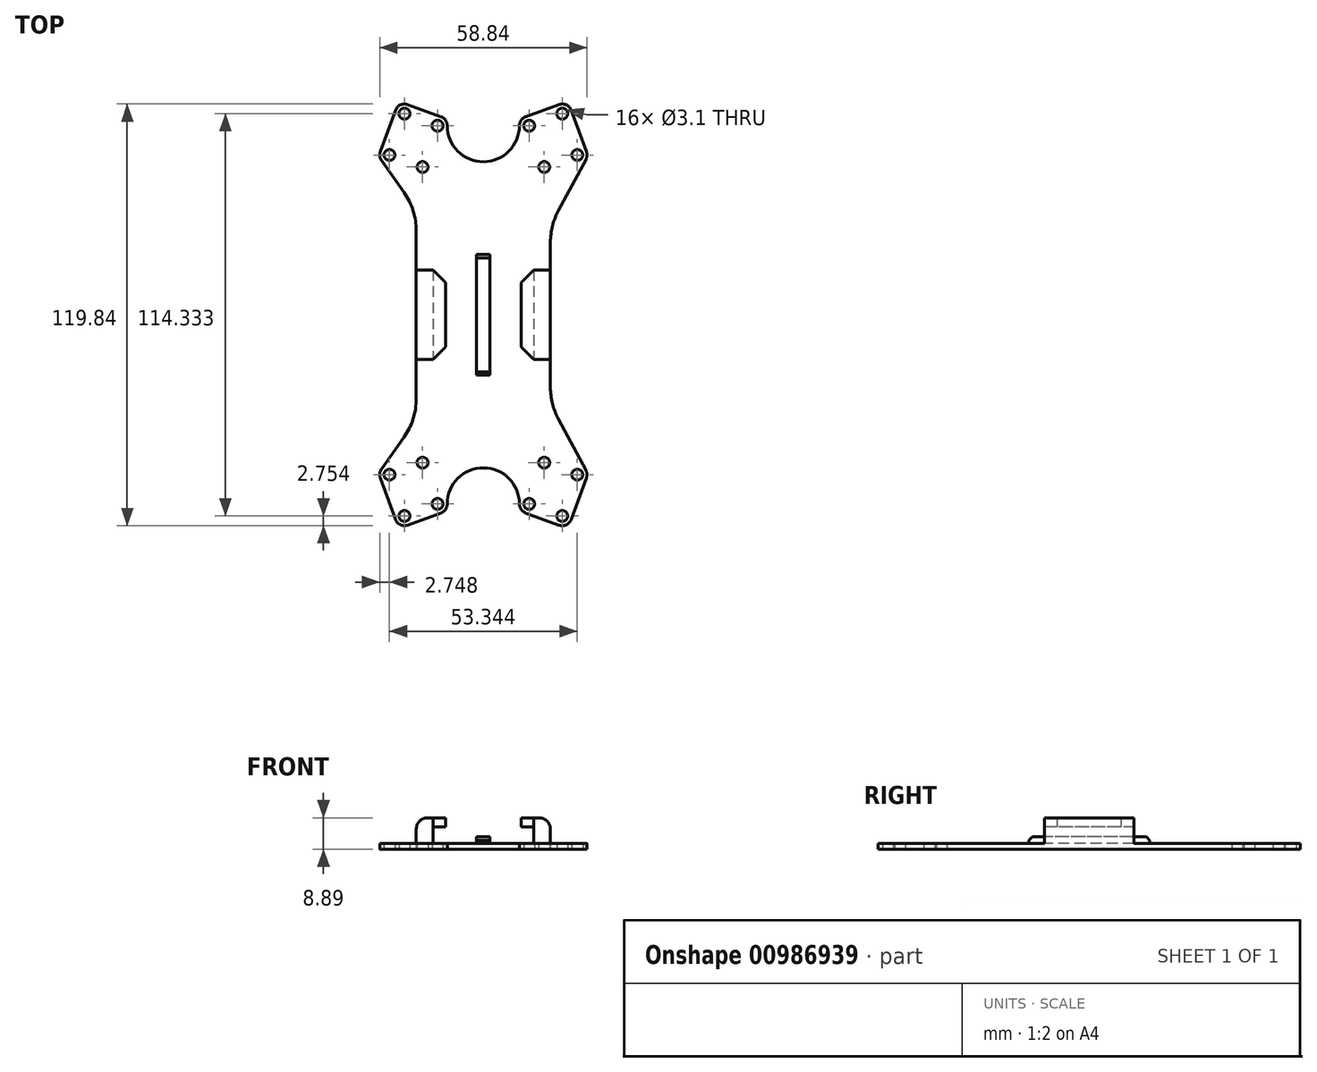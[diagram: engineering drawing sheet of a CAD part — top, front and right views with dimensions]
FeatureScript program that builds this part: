
annotation { "Feature Type Name" : "Feature", "Feature Type Description" : "" }
export const myFeature = defineFeature(function(context is Context, id is Id, definition is map)
    precondition{}
    {
        {
            var Q0;
            Q0=qCreatedBy(makeId("Top.planeOp"),FACE);
            var sketch = newSketch(context, id + "F0", { "sketchPlane" : qUnion([Q0])});
            skCircle(sketch, "E0", {"center": v(-22.4, 57.17) * mm, "radius": 1.55 * mm});
            skCircle(sketch, "E1", {"center": v(-13, 53.75) * mm, "radius": 1.55 * mm});
            skCircle(sketch, "E2", {"center": v(-17.28, 42) * mm, "radius": 1.55 * mm});
            skCircle(sketch, "E3", {"center": v(-26.67, 45.42) * mm, "radius": 1.55 * mm});
            skArc(sketch, "E4.0", {"start": v(-10.25, 53.75) * mm, "mid": v(-10.75, 55.32) * mm, "end": v(-12.06, 56.33) * mm});
            skArc(sketch, "E5.0", {"start": v(-21.46, 59.75) * mm, "mid": v(-23.56, 59.66) * mm, "end": v(-24.98, 58.1) * mm});
            skArc(sketch, "E6.0", {"start": v(-29.26, 46.36) * mm, "mid": v(-29.4, 45.06) * mm, "end": v(-28.92, 43.83) * mm});
            skArc(sketch, "E7.MirrorCS", {"start": v(29.26, 46.36) * mm, "mid": v(29.42, 45.22) * mm, "end": v(29.1, 44.12) * mm});
            skArc(sketch, "E8.MirrorCS", {"start": v(21.46, 59.75) * mm, "mid": v(23.56, 59.66) * mm, "end": v(24.98, 58.1) * mm});
            skCircle(sketch, "E9.MirrorC", {"center": v(17.28, 42) * mm, "radius": 1.55 * mm});
            skArc(sketch, "E10.MirrorCS", {"start": v(10.25, 53.75) * mm, "mid": v(10.75, 55.32) * mm, "end": v(12.06, 56.33) * mm});
            skCircle(sketch, "E11.MirrorC", {"center": v(13, 53.75) * mm, "radius": 1.55 * mm});
            skCircle(sketch, "E12.MirrorC", {"center": v(26.67, 45.42) * mm, "radius": 1.55 * mm});
            skCircle(sketch, "E13.MirrorC", {"center": v(22.4, 57.17) * mm, "radius": 1.55 * mm});
            skArc(sketch, "E14", {"start": v(-10.25, 53.75) * mm, "mid": v(0, 43.5) * mm, "end": v(10.25, 53.75) * mm});
            skLineSegment(sketch, "E15", {"start": v(-19.05, 0) * mm, "end": v(19.05, 0) * mm});
            skLineSegment(sketch, "E16", {"start": v(-19.05, 0) * mm, "end": v(-19.05, 23.8) * mm});
            skLineSegment(sketch, "E17", {"start": v(19.05, 0) * mm, "end": v(19.05, 20.61) * mm});
            skLineSegment(sketch, "E18", {"start": v(21.31, 29.62) * mm, "end": v(29.1, 44.12) * mm});
            skLineSegment(sketch, "E19", {"start": v(-22.53, 34.79) * mm, "end": v(-28.92, 43.83) * mm});
            skPoint(sketch, "E20.visualSharp", {"position": v(-19.05, 29.85) * mm});
            skArc(sketch, "E20.filletArc", {"start": v(-19.05, 23.8) * mm, "mid": v(-19.94, 29.57) * mm, "end": v(-22.53, 34.79) * mm});
            skPoint(sketch, "E21.visualSharp", {"position": v(19.05, 25.4) * mm});
            skArc(sketch, "E21.filletArc", {"start": v(21.31, 29.62) * mm, "mid": v(19.62, 25.26) * mm, "end": v(19.05, 20.61) * mm});
            skLineSegment(sketch, "E22", {"start": v(-29.26, 46.36) * mm, "end": v(-24.98, 58.1) * mm});
            skLineSegment(sketch, "E23", {"start": v(-21.46, 59.75) * mm, "end": v(-12.06, 56.33) * mm});
            skLineSegment(sketch, "E24", {"start": v(29.26, 46.36) * mm, "end": v(24.98, 58.1) * mm});
            skLineSegment(sketch, "E25", {"start": v(21.46, 59.75) * mm, "end": v(12.06, 56.33) * mm});
            skSolve(sketch);
        }
        {
            var Q0;
            Q0=makeQuery(id+"F0.imprint","IMPRINT",FACE,{"disambiguationData":[TD([[makeQuery(id+"F0.imprint","IMPRINT",EDGE,{"derivedFrom":sQuery(id+"F0.wireOp",EDGE,"E7.MirrorCS")}),-1.0]])]});
            var Q1;
            Q1=makeQuery(id+"F0.imprint","IMPRINT",FACE,{"disambiguationData":[TD([[makeQuery(id+"F0.imprint","IMPRINT",EDGE,{"derivedFrom":sQuery(id+"F0.wireOp",EDGE,"E0")}),-1.0]])]});
            var Q2;
            {var subQ6=sQuery(id+"F0.wireOp",EDGE,"199f6d11-cf79-4d1c-950d-0f2b3a67f5500.MirrorCS");Q2=makeQuery(id+"F0.imprint","IMPRINT",FACE,{"disambiguationData":[TD([[makeQuery(id+"F0.imprint","IMPRINT",EDGE,{"derivedFrom":subQ6}),-1.0]])]});}
            var Q3;
            Q3=makeQuery(id+"F0.imprint","IMPRINT",FACE,{"disambiguationData":[TD([[makeQuery(id+"F0.imprint","IMPRINT",EDGE,{"derivedFrom":sQuery(id+"F0.wireOp",EDGE,"199f6d11-cf79-4d1c-950d-0f2b3a67f5509.MirrorC")}),-1.0]])]});
            extrude(context, id + "F1", {"entities" : qUnion([Q0, Q1, Q2, Q3]), "depth" : 3.17 * mm, "offsetDistance" : 25.4 * mm});
        }
        {
            var Q0;
            Q0=makeQuery(id+"F1.opExtrude","SWEPT_FACE",FACE,{"disambiguationData":[OSD([sQuery(id+"F0.wireOp",EDGE,"E15")])]});
            var sketch = newSketch(context, id + "F2", { "sketchPlane" : qUnion([Q0])});
            skLineSegment(sketch, "E26", {"start": v(-14.29, 3.18) * mm, "end": v(-1.9, 3.18) * mm});
            skLineSegment(sketch, "E27", {"start": v(-14.29, 3.18) * mm, "end": v(-14.29, 7.94) * mm});
            skLineSegment(sketch, "E28", {"start": v(14.29, 3.18) * mm, "end": v(14.29, 7.94) * mm});
            skLineSegment(sketch, "E29", {"start": v(14.29, 7.94) * mm, "end": v(10.73, 7.94) * mm});
            skLineSegment(sketch, "E30", {"start": v(-14.29, 7.94) * mm, "end": v(-10.73, 7.94) * mm});
            skLineSegment(sketch, "E31", {"start": v(-1.9, 5.08) * mm, "end": v(1.9, 5.08) * mm});
            skLineSegment(sketch, "E32", {"start": v(-1.9, 5.08) * mm, "end": v(-1.9, 3.18) * mm});
            skLineSegment(sketch, "E33", {"start": v(1.9, 5.08) * mm, "end": v(1.9, 3.18) * mm});
            skLineSegment(sketch, "E34", {"start": v(-10.73, 7.94) * mm, "end": v(-10.73, 10.48) * mm});
            skLineSegment(sketch, "E35", {"start": v(10.73, 7.94) * mm, "end": v(10.73, 10.48) * mm});
            skLineSegment(sketch, "E36", {"start": v(19.05, 3.18) * mm, "end": v(19.05, 10.48) * mm});
            skLineSegment(sketch, "E37", {"start": v(10.73, 10.48) * mm, "end": v(19.05, 10.48) * mm});
            skLineSegment(sketch, "E38.0", {"start": v(-19.05, 10.48) * mm, "end": v(-10.73, 10.48) * mm});
            skLineSegment(sketch, "E39.0", {"start": v(-19.05, 3.18) * mm, "end": v(-19.05, 10.48) * mm});
            skLineSegment(sketch, "E40.trimOffspring", {"start": v(1.9, 3.18) * mm, "end": v(14.29, 3.18) * mm});
            skLineSegment(sketch, "E41", {"start": v(19.05, 3.18) * mm, "end": v(-19.05, 3.18) * mm});
            skSolve(sketch);
        }
        {
            var Q0;
            Q0 = qSketchRegion(id + "F2", true);
            extrude(context, id + "F3", {"entities" : qUnion([Q0]), "operationType" : NewBodyOperationType.ADD, "oppositeDirection" : true, "depth" : 12.7 * mm, "offsetDistance" : 25.4 * mm});
        }
        {
            var Q0;
            Q0=makeQuery(id+"F1.opExtrude","SWEPT_BODY",BODY,{"disambiguationData":[OSD([sQuery(id+"F0.wireOp",EDGE,"E0"),sQuery(id+"F0.wireOp",EDGE,"E1"),sQuery(id+"F0.wireOp",EDGE,"E2"),sQuery(id+"F0.wireOp",EDGE,"E3"),sQuery(id+"F0.wireOp",EDGE,"165232c8-0929-413c-b805-239f1ec5fdc3.0"),sQuery(id+"F0.wireOp",EDGE,"E4.0"),sQuery(id+"F0.wireOp",EDGE,"E5.0"),sQuery(id+"F0.wireOp",EDGE,"E6.0"),sQuery(id+"F0.wireOp",EDGE,"AX0kzdIw-M9t9-PeBU-QoqW-9dPJvJCT8jwo"),sQuery(id+"F0.wireOp",EDGE,"eeiW39AE-7Khv-Netx-21Ry-1MclAGHMc0yk"),sQuery(id+"F0.wireOp",EDGE,"f2INQ4ec-qhfp-OF0n-tSpk-pPh30l36Cp4f"),sQuery(id+"F0.wireOp",EDGE,"E7.MirrorCS"),sQuery(id+"F0.wireOp",EDGE,"E8.MirrorCS"),sQuery(id+"F0.wireOp",EDGE,"E9.MirrorC"),sQuery(id+"F0.wireOp",EDGE,"E10.MirrorCS"),sQuery(id+"F0.wireOp",EDGE,"E11.MirrorC"),sQuery(id+"F0.wireOp",EDGE,"f3ecabe8-481c-4a03-a0b0-112aaabd95ab5.MirrorCS"),sQuery(id+"F0.wireOp",EDGE,"f3ecabe8-481c-4a03-a0b0-112aaabd95ab6.MirrorCS"),sQuery(id+"F0.wireOp",EDGE,"E12.MirrorC"),sQuery(id+"F0.wireOp",EDGE,"E13.MirrorC"),sQuery(id+"F0.wireOp",EDGE,"f3ecabe8-481c-4a03-a0b0-112aaabd95ab9.MirrorCS"),sQuery(id+"F0.wireOp",EDGE,"E80.MirrorCS"),sQuery(id+"F0.wireOp",EDGE,"E14"),sQuery(id+"F0.wireOp",EDGE,"E15"),sQuery(id+"F0.wireOp",EDGE,"E16"),sQuery(id+"F0.wireOp",EDGE,"NEXEyMZG-Vf1b-1tYN-iwbf-hq2jZdTpUJsp"),sQuery(id+"F0.wireOp",EDGE,"E17"),sQuery(id+"F0.wireOp",EDGE,"hQ4HOrQn-tPb4-Rm9s-gEcP-knbR1JslG5sg")])]});
            var Q1;
            {var subQ0=sQuery(id+"F2.wireOp",EDGE,"E41");Q1=makeQuery(id+"F3.boolean.opBoolean","MERGE",FACE,{"derivedFrom":[makeQuery(id+"F1.opExtrude","SWEPT_FACE",FACE,{"disambiguationData":[OSD([sQuery(id+"F0.wireOp",EDGE,"E15")])]}),makeQuery(id+"F3.opExtrude","CAP_FACE",FACE,{"disambiguationData":[OSD([sQuery(id+"F2.wireOp",EDGE,"E27"),sQuery(id+"F2.wireOp",EDGE,"E30"),sQuery(id+"F2.wireOp",EDGE,"E34"),sQuery(id+"F2.wireOp",EDGE,"E38.0"),sQuery(id+"F2.wireOp",EDGE,"E39.0"),subQ0])],"isStart":true}),makeQuery(id+"F3.opExtrude","CAP_FACE",FACE,{"disambiguationData":[OSD([sQuery(id+"F2.wireOp",EDGE,"E28"),sQuery(id+"F2.wireOp",EDGE,"E29"),sQuery(id+"F2.wireOp",EDGE,"E35"),sQuery(id+"F2.wireOp",EDGE,"E36"),sQuery(id+"F2.wireOp",EDGE,"E37"),subQ0])],"isStart":true}),makeQuery(id+"F3.opExtrude","CAP_FACE",FACE,{"disambiguationData":[OSD([sQuery(id+"F2.wireOp",EDGE,"E31"),sQuery(id+"F2.wireOp",EDGE,"E32"),sQuery(id+"F2.wireOp",EDGE,"E33"),subQ0])],"isStart":true})]});}
            mirror(context, id + "F4", {"operationType" : NewBodyOperationType.ADD, "entities" : qUnion([Q0]), "mirrorPlane" : qUnion([Q1])});
        }
        {
            var Q0;
            Q0=makeQuery(id+"F4.opPattern","COPY",EDGE,{"derivedFrom":makeQuery(id+"F3.opExtrude","CAP_EDGE",EDGE,{"disambiguationData":[OSD([sQuery(id+"F2.wireOp",EDGE,"E35")])],"isStart":false}),"instanceName":"1"});
            var Q1;
            Q1=makeQuery(id+"F4.opPattern","COPY",EDGE,{"derivedFrom":makeQuery(id+"F3.opExtrude","CAP_EDGE",EDGE,{"disambiguationData":[OSD([sQuery(id+"F2.wireOp",EDGE,"E34")])],"isStart":false}),"instanceName":"1"});
            var Q2;
            Q2=makeQuery(id+"F3.opExtrude","CAP_EDGE",EDGE,{"disambiguationData":[OSD([sQuery(id+"F2.wireOp",EDGE,"E34")])],"isStart":false});
            var Q3;
            Q3=makeQuery(id+"F3.opExtrude","CAP_EDGE",EDGE,{"disambiguationData":[OSD([sQuery(id+"F2.wireOp",EDGE,"E35")])],"isStart":false});
            chamfer(context, id + "F5", {"entities" : qUnion([Q0, Q1, Q2, Q3]), "width" : 3.56 * mm, "tangentPropagation" : true});
        }
        {
            var Q0;
            Q0=makeQuery(id+"F4.opPattern","COPY",FACE,{"derivedFrom":makeQuery(id+"F3.opExtrude","CAP_FACE",FACE,{"disambiguationData":[OSD([sQuery(id+"F2.wireOp",EDGE,"E31"),sQuery(id+"F2.wireOp",EDGE,"E32"),sQuery(id+"F2.wireOp",EDGE,"E33"),sQuery(id+"F2.wireOp",EDGE,"E41")])],"isStart":false}),"instanceName":"1"});
            extrude(context, id + "F6", {"entities" : qUnion([Q0]), "operationType" : NewBodyOperationType.ADD, "depth" : 4.44 * mm, "offsetDistance" : 25.4 * mm});
        }
        {
            var Q0;
            Q0=makeQuery(id+"F3.opExtrude","CAP_FACE",FACE,{"disambiguationData":[OSD([sQuery(id+"F2.wireOp",EDGE,"E31"),sQuery(id+"F2.wireOp",EDGE,"E32"),sQuery(id+"F2.wireOp",EDGE,"E33"),sQuery(id+"F2.wireOp",EDGE,"E41")])],"isStart":false});
            extrude(context, id + "F7", {"entities" : qUnion([Q0]), "operationType" : NewBodyOperationType.ADD, "depth" : 4.44 * mm, "offsetDistance" : 25.4 * mm});
        }
        {
            var Q0;
            Q0=makeQuery(id+"F7.opExtrude","CAP_EDGE",EDGE,{"disambiguationData":[OSD([sQuery(id+"F2.wireOp",EDGE,"E31")])],"isStart":false});
            var Q1;
            Q1=makeQuery(id+"F6.opExtrude","CAP_EDGE",EDGE,{"disambiguationData":[OSD([sQuery(id+"F2.wireOp",EDGE,"E31")])],"isStart":false});
            chamfer(context, id + "F8", {"entities" : qUnion([Q0, Q1]), "width" : 0.95 * mm, "tangentPropagation" : true});
        }
        {
            var Q0;
            {var subQ0=makeQuery(id+"F1.opExtrude","CAP_FACE",FACE,{"disambiguationData":[OSD([sQuery(id+"F0.wireOp",EDGE,"E0"),sQuery(id+"F0.wireOp",EDGE,"E1"),sQuery(id+"F0.wireOp",EDGE,"E2"),sQuery(id+"F0.wireOp",EDGE,"E3"),sQuery(id+"F0.wireOp",EDGE,"165232c8-0929-413c-b805-239f1ec5fdc3.0"),sQuery(id+"F0.wireOp",EDGE,"E4.0"),sQuery(id+"F0.wireOp",EDGE,"E5.0"),sQuery(id+"F0.wireOp",EDGE,"E6.0"),sQuery(id+"F0.wireOp",EDGE,"AX0kzdIw-M9t9-PeBU-QoqW-9dPJvJCT8jwo"),sQuery(id+"F0.wireOp",EDGE,"eeiW39AE-7Khv-Netx-21Ry-1MclAGHMc0yk"),sQuery(id+"F0.wireOp",EDGE,"f2INQ4ec-qhfp-OF0n-tSpk-pPh30l36Cp4f"),sQuery(id+"F0.wireOp",EDGE,"E7.MirrorCS"),sQuery(id+"F0.wireOp",EDGE,"E8.MirrorCS"),sQuery(id+"F0.wireOp",EDGE,"E9.MirrorC"),sQuery(id+"F0.wireOp",EDGE,"E10.MirrorCS"),sQuery(id+"F0.wireOp",EDGE,"E11.MirrorC"),sQuery(id+"F0.wireOp",EDGE,"f3ecabe8-481c-4a03-a0b0-112aaabd95ab5.MirrorCS"),sQuery(id+"F0.wireOp",EDGE,"f3ecabe8-481c-4a03-a0b0-112aaabd95ab6.MirrorCS"),sQuery(id+"F0.wireOp",EDGE,"E12.MirrorC"),sQuery(id+"F0.wireOp",EDGE,"E13.MirrorC"),sQuery(id+"F0.wireOp",EDGE,"f3ecabe8-481c-4a03-a0b0-112aaabd95ab9.MirrorCS"),sQuery(id+"F0.wireOp",EDGE,"E80.MirrorCS"),sQuery(id+"F0.wireOp",EDGE,"E14"),sQuery(id+"F0.wireOp",EDGE,"E15"),sQuery(id+"F0.wireOp",EDGE,"E16"),sQuery(id+"F0.wireOp",EDGE,"NEXEyMZG-Vf1b-1tYN-iwbf-hq2jZdTpUJsp"),sQuery(id+"F0.wireOp",EDGE,"E17"),sQuery(id+"F0.wireOp",EDGE,"hQ4HOrQn-tPb4-Rm9s-gEcP-knbR1JslG5sg")])],"isStart":true});Q0=makeQuery(id+"F4.boolean.opBoolean","MERGE",FACE,{"derivedFrom":[subQ0,makeQuery(id+"F4.opPattern","COPY",FACE,{"derivedFrom":subQ0,"instanceName":"1"})]});}
            extrude(context, id + "F9", {"entities" : qUnion([Q0]), "operationType" : NewBodyOperationType.REMOVE, "oppositeDirection" : true, "depth" : 1.59 * mm, "offsetDistance" : 25.4 * mm});
        }
        {
            var Q0;
            {var subQ0=makeQuery(id+"F3.opExtrude","SWEPT_EDGE",EDGE,{"disambiguationData":[OSD([sQuery(id+"F2.wireOp",EDGE,"E38.0"),sQuery(id+"F2.wireOp",EDGE,"E39.0")])]});Q0=makeQuery(id+"F4.boolean.opBoolean","MERGE",EDGE,{"derivedFrom":[subQ0,makeQuery(id+"F4.opPattern","COPY",EDGE,{"derivedFrom":subQ0,"instanceName":"1"})]});}
            var Q1;
            {var subQ0=makeQuery(id+"F3.opExtrude","SWEPT_EDGE",EDGE,{"disambiguationData":[OSD([sQuery(id+"F2.wireOp",EDGE,"E36"),sQuery(id+"F2.wireOp",EDGE,"E37")])]});Q1=makeQuery(id+"F4.boolean.opBoolean","MERGE",EDGE,{"derivedFrom":[subQ0,makeQuery(id+"F4.opPattern","COPY",EDGE,{"derivedFrom":subQ0,"instanceName":"1"})]});}
            fillet(context, id + "F10", {"entities" : qUnion([Q0, Q1]), "radius" : 3.17 * mm, "tangentPropagation" : true, "allowEdgeOverflow" : false});
        }
    });
